# Revit family: PRD_AR_MltFnctnDspnsrs_RODANPaperTowelWasteBinCombination_RODX602_RODX602E
name_source: partatom
category: Specialty Equipment
revit_build: Autodesk Revit 2018 (Build: 20190510_1515(x64)
units: mm (PartAtom-declared; Revit-internal decimal feet)

## family parameters
Cut with Voids When Loaded = Yes
Host = Face
OmniClass Number = 23.40.20.21.17
OmniClass Title = Paper Towel Dispensers, Disposal Units
Part Type = Normal
Room Calculation Point = No
Round Connector Dimension = Use Diameter
Shared = No

## types (2) — shared parameters
AssetType = Fixed
Category = Pr_40_70_22_52, Multi-function dispensers
CombinationPart1 = Paper towel dispenser
CombinationPart2 = Waste bin
Default Elevation = 800 mm  [stored 2.62467 ft]
DispenserMaterial = PRD_AR_StainlessSteel_SatinFinished
DurationUnit = year
Features = stainless steel, surface satin finished
FillingQuantity1 = 800
FillingQuantity1Uom = Pieces
FillingQuantity2 = 23
FillingQuantity2Uom = Liter
Finish = satin finished
IfcExportAs = IfcFurnitureType
IfcExportType = USERDEFINED
IntegralAccessories = incl. stainless steel screws and dowels
IsBuiltIn = TRUE
Lock1 = Key-lock
Lock2 = Key-lock
MainColor = stainless steel
Manufacturer = KWC Group AG
ManufacturerName = KWC Group AG
ManufacturerURL = www.kwc.com
Material = stainless steel
MaterialCode = 1.4301
MaterialThickness = 0.80 mm
NBSDescription = Multi-function dispensers
NBSReference = 45-35-72/384
ProductInformation = https://pim.kwc.com
TypeOfConsumable1 = Paper towel
TypeOfFixing = Screw
URL = www.kwc.com
Uniclass2015Code = Pr_40_70_22_52
Uniclass2015Title = Multi-function dispensers
Uniclass2015Version = Products v1.10
Version = 1
WarrantyDurationUnit = year

## per-type parameters (varying)
| type | BIMObjectName | Description | GrossWeight | ModelNumber | ModelOffset | Name | NetWeight | NominalDepth | NominalHeight | NominalWidth | Size | TypeOfMounting | VoidOffset |
| RODX602 | PRD_AR_MultiFunctionDispensers_RODANPaperTowelWasteBinCombination_RODX602 | Paper towel dispenser, waste bin combination for wall mounting, stainless steel, surface satin finished, material thickness 0.8 mm, folded front cover, cylinder lock with KWC standard key, loading capacity 500 - 800 pcs. of paper depending on convolution, waste bin with approx. 23 liter capacity, inclusive stainless steel screws and dowels. | 16.27 kg | 2000090059 | 114 mm  [stored 0.374016 ft] | Paper Towel Waste Bin Combination RODX602 | 14.42 kg | 171 mm  [stored 0.561024 ft] | 1148 mm  [stored 3.7664 ft] | 411 mm  [stored 1.34843 ft] | 411 x 1148 x 171 mm | Wall mounting | 150 mm |
| RODX602E | PRD_AR_MultiFunctionDispensers_RODANPaperTowelWasteBinCombination_RODX602E | Paper towel dispenser - waste bin combination for recessed mounting, stainless steel, surface satin finished, material thickness 0.8 mm, folded front cover, cylinder lock with KWC standard key, loading capacity 500 - 800 pcs. of paper depending on convolution, waste bin with approx. 23 liter capacity, includes stainless steel screws and dowels. | 12.68 kg | 2000090060 | 0 mm  [stored 0 ft] | Paper Towel Waste Bin Combination RODX602E | 10.60 kg | 169 mm  [stored 0.554462 ft] | 1145 mm  [stored 3.75656 ft] | 408 mm | 408 x 1145 x 169 mm | Recessed mounting | 36 mm  [stored 0.11811 ft] |

note: column(s) folded — value = type name in every type: Model, ModelReference, Type

note: [stored X ft] marks values corroborated as IEEE doubles in the binary element streams (Revit-internal decimal feet)

## geometry (parser evidence)
native form markers: Sweep x2
no freeform markers — native parametric forms only
